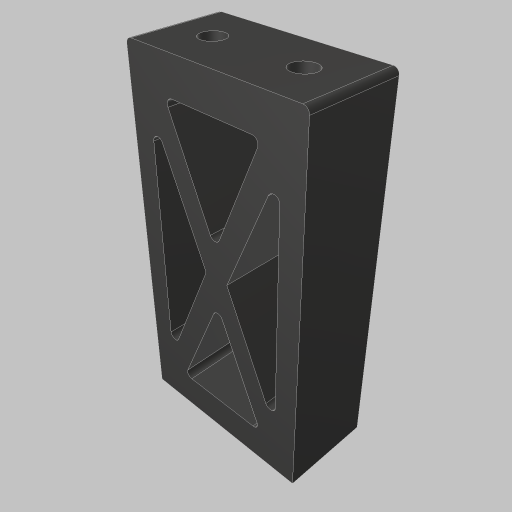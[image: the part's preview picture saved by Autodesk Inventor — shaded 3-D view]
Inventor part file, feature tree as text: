
AUTODESK INVENTOR PART (.ipt)
format: ipt  version: 2023.5 (Build 275446000, 446)  size: 239,104 bytes
history: native  units: in
note: dims shown in document units (in); Inventor stores cm internally (conversion verified against a paired STEP export)
features: sketch x4, extrude x2, hole x2, projected_geometry x2, fillet x1
ambient origin geometry x8: Origin, YZ Plane, XZ Plane, XY Plane, X Axis, Y Axis, Z Axis, Center Point
bodies: Solid1 (feature_tree)
feature tree (11):
  extrude  "Extrusion1"  Depth=1.0in
  extrude  "Extrusion2"  Depth=0.25in
  fillet  "Fillet1"  Radius=0.125in
  hole  "Hole1"  [1 undecoded]
  hole  "Hole2"  [1 undecoded]
  sketch  "Sketch1"  dims[d0=2.0in d1=1.0in]
  sketch  "Sketch2"  dims[d2=3.9in d3=0.0in d4=0.25in d5=0.125in]
  sketch  "Sketch3"  dims[d6=0.125in d7=0.125in]
  sketch  "Sketch4"  dims[d8=0.125in d9=0.385in d10=0.0in d11=0.0in d12=0.5in d13=0.5in d14=0.5in d15=0.2657in d16=0.75in d17=0.385in d18=0.25in d19=0.5635in d20=0.375in d21=0.0in d22=0.0625in d23=0.385in d24=1.0in d25=0.2657in d26=0.75in d27=0.375in d28=0.25in d29=0.5635in d30=0.375in d31=0.0in]
  projected_geometry  "Project Cut Edges1"
  projected_geometry  "Project Cut Edges2"
note: 2 required parameter values undecoded (feature->parameter linkage not recoverable at this tier; creation-order binding heuristic only, values carry confidence <= 0.55)
